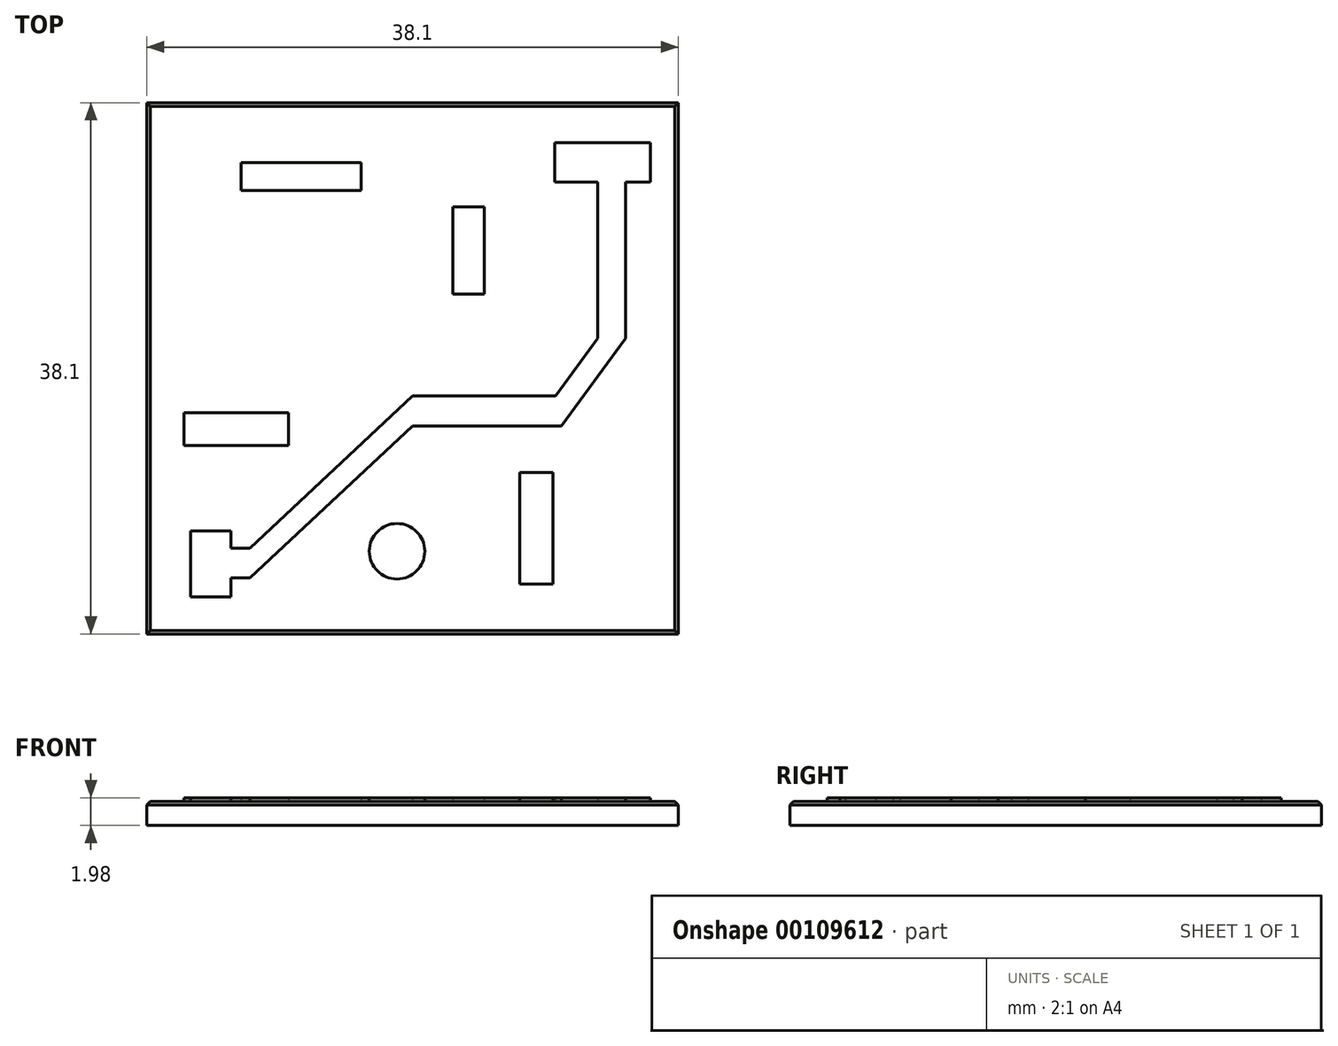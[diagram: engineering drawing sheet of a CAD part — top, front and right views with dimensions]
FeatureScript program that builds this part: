
annotation { "Feature Type Name" : "Feature", "Feature Type Description" : "" }
export const myFeature = defineFeature(function(context is Context, id is Id, definition is map)
    precondition{}
    {
        {
            var Q0;
            Q0=qCreatedBy(makeId("Top.planeOp"),FACE);
            var sketch = newSketch(context, id + "F0", { "sketchPlane" : qUnion([Q0])});
            skLineSegment(sketch, "E0.bottom", {"start": v(19.05, 19.05) * mm, "end": v(-19.05, 19.05) * mm});
            skLineSegment(sketch, "E0.top", {"start": v(19.05, -19.05) * mm, "end": v(-19.05, -19.05) * mm});
            skLineSegment(sketch, "E0.left", {"start": v(19.05, 19.05) * mm, "end": v(19.05, -19.05) * mm});
            skLineSegment(sketch, "E0.right", {"start": v(-19.05, 19.05) * mm, "end": v(-19.05, -19.05) * mm});
            skPoint(sketch, "E0.middle", {"position": v(0, 0) * mm});
            skSolve(sketch);
        }
        {
            var Q0;
            Q0=makeQuery(id+"F0.imprint","IMPRINT",FACE,{"disambiguationData":[TD([[makeQuery(id+"F0.imprint","IMPRINT",EDGE,{"derivedFrom":sQuery(id+"F0.wireOp",EDGE,"E0.bottom")}),1.0]])]});
            extrude(context, id + "F1", {"entities" : qUnion([Q0]), "depth" : 1.73 * mm});
        }
        {
            var Q0;
            Q0=makeQuery(id+"F1.opExtrude","CAP_EDGE",EDGE,{"disambiguationData":[OSD([sQuery(id+"F0.wireOp",EDGE,"E0.top")])],"isStart":false});
            var Q1;
            Q1=makeQuery(id+"F1.opExtrude","CAP_EDGE",EDGE,{"disambiguationData":[OSD([sQuery(id+"F0.wireOp",EDGE,"E0.right")])],"isStart":false});
            var Q2;
            Q2=makeQuery(id+"F1.opExtrude","CAP_EDGE",EDGE,{"disambiguationData":[OSD([sQuery(id+"F0.wireOp",EDGE,"E0.bottom")])],"isStart":false});
            var Q3;
            Q3=makeQuery(id+"F1.opExtrude","CAP_EDGE",EDGE,{"disambiguationData":[OSD([sQuery(id+"F0.wireOp",EDGE,"E0.left")])],"isStart":false});
            chamfer(context, id + "F2", {"entities" : qUnion([Q0, Q1, Q2, Q3]), "width" : 0.25 * mm, "tangentPropagation" : true});
        }
        {
            var Q0;
            Q0=makeQuery(id+"F1.opExtrude","CAP_FACE",FACE,{"disambiguationData":[OSD([sQuery(id+"F0.wireOp",EDGE,"E0.bottom"),sQuery(id+"F0.wireOp",EDGE,"E0.top"),sQuery(id+"F0.wireOp",EDGE,"E0.left"),sQuery(id+"F0.wireOp",EDGE,"E0.right")])],"isStart":false});
            var sketch = newSketch(context, id + "F3", { "sketchPlane" : qUnion([Q0])});
            skLineSegment(sketch, "E1.bottom", {"start": v(-15.9, -11.66) * mm, "end": v(-13, -11.66) * mm});
            skLineSegment(sketch, "E1.top", {"start": v(-15.9, -16.4) * mm, "end": v(-13, -16.4) * mm});
            skLineSegment(sketch, "E1.left", {"start": v(-15.9, -11.66) * mm, "end": v(-15.9, -16.4) * mm});
            skLineSegment(sketch, "E1.right", {"start": v(-13, -11.66) * mm, "end": v(-13, -16.4) * mm});
            skLineSegment(sketch, "E2", {"start": v(-13, -12.89) * mm, "end": v(-11.65, -12.89) * mm});
            skLineSegment(sketch, "E3", {"start": v(-13, -14.03) * mm, "end": v(-11.65, -14.03) * mm});
            skLineSegment(sketch, "E4", {"start": v(-13, -15.04) * mm, "end": v(-11.65, -15.04) * mm});
            skLineSegment(sketch, "E5", {"start": v(-11.65, -12.89) * mm, "end": v(0, -1.98) * mm});
            skLineSegment(sketch, "E6", {"start": v(-11.65, -14.03) * mm, "end": v(0, -3.12) * mm});
            skLineSegment(sketch, "E7", {"start": v(-11.65, -15.04) * mm, "end": v(0, -4.13) * mm});
            skLineSegment(sketch, "E8", {"start": v(0, -1.98) * mm, "end": v(10.25, -1.98) * mm});
            skLineSegment(sketch, "E9", {"start": v(0, -4.13) * mm, "end": v(10.67, -4.13) * mm});
            skLineSegment(sketch, "E10", {"start": v(0, -3.12) * mm, "end": v(10.67, -3.12) * mm});
            skLineSegment(sketch, "E11.bottom", {"start": v(10.19, 16.17) * mm, "end": v(17.05, 16.17) * mm});
            skLineSegment(sketch, "E11.top", {"start": v(10.19, 13.37) * mm, "end": v(17.05, 13.37) * mm});
            skLineSegment(sketch, "E11.left", {"start": v(10.19, 16.17) * mm, "end": v(10.19, 13.37) * mm});
            skLineSegment(sketch, "E11.right", {"start": v(17.05, 16.17) * mm, "end": v(17.05, 13.37) * mm});
            skLineSegment(sketch, "E12", {"start": v(12.03, 13.37) * mm, "end": v(12.03, 11.34) * mm});
            skLineSegment(sketch, "E13", {"start": v(13.28, 13.37) * mm, "end": v(13.28, 11.34) * mm});
            skLineSegment(sketch, "E14", {"start": v(15.27, 13.37) * mm, "end": v(15.27, 11.52) * mm});
            skLineSegment(sketch, "E15", {"start": v(14.54, 13.37) * mm, "end": v(14.54, 11.34) * mm});
            skLineSegment(sketch, "E16", {"start": v(15.27, 11.52) * mm, "end": v(15.27, 2.14) * mm});
            skLineSegment(sketch, "E17", {"start": v(15.27, 2.14) * mm, "end": v(10.67, -4.13) * mm});
            skLineSegment(sketch, "E18", {"start": v(14.54, 11.34) * mm, "end": v(14.54, 2.15) * mm});
            skLineSegment(sketch, "E19", {"start": v(14.54, 2.15) * mm, "end": v(10.67, -3.12) * mm});
            skLineSegment(sketch, "E20", {"start": v(13.28, 11.34) * mm, "end": v(13.28, 2.15) * mm});
            skLineSegment(sketch, "E21", {"start": v(13.28, 2.15) * mm, "end": v(10.25, -1.98) * mm});
            skLineSegment(sketch, "E22", {"start": v(12.03, 11.34) * mm, "end": v(4, 2.25) * mm});
            skLineSegment(sketch, "E23", {"start": v(4, 2.25) * mm, "end": v(-10.6, 2.25) * mm});
            skLineSegment(sketch, "E24", {"start": v(-10.6, 2.25) * mm, "end": v(-15.44, 6.7) * mm});
            skLineSegment(sketch, "E25", {"start": v(-15.44, 6.7) * mm, "end": v(-15.44, 18.8) * mm});
            skPoint(sketch, "E26.oppositeSnap0", {"position": v(-15.44, 12.75) * mm});
            skLineSegment(sketch, "E26.bottom", {"start": v(-12.28, 14.75) * mm, "end": v(-3.67, 14.75) * mm});
            skLineSegment(sketch, "E26.top", {"start": v(-12.28, 12.75) * mm, "end": v(-3.67, 12.75) * mm});
            skLineSegment(sketch, "E26.left", {"start": v(-12.28, 14.75) * mm, "end": v(-12.28, 12.75) * mm});
            skLineSegment(sketch, "E26.right", {"start": v(-3.67, 14.75) * mm, "end": v(-3.67, 12.75) * mm});
            skLineSegment(sketch, "E27.bottom", {"start": v(7.7, -7.49) * mm, "end": v(10.05, -7.49) * mm});
            skLineSegment(sketch, "E27.top", {"start": v(7.7, -15.48) * mm, "end": v(10.05, -15.48) * mm});
            skLineSegment(sketch, "E27.left", {"start": v(7.7, -7.49) * mm, "end": v(7.7, -15.48) * mm});
            skLineSegment(sketch, "E27.right", {"start": v(10.05, -7.49) * mm, "end": v(10.05, -15.48) * mm});
            skLineSegment(sketch, "E28.bottom", {"start": v(-8.9, -3.18) * mm, "end": v(-16.38, -3.18) * mm});
            skLineSegment(sketch, "E28.top", {"start": v(-8.9, -5.54) * mm, "end": v(-16.38, -5.54) * mm});
            skLineSegment(sketch, "E28.left", {"start": v(-8.9, -3.18) * mm, "end": v(-8.9, -5.54) * mm});
            skLineSegment(sketch, "E28.right", {"start": v(-16.38, -3.18) * mm, "end": v(-16.38, -5.54) * mm});
            skLineSegment(sketch, "E29.bottom", {"start": v(2.88, 11.57) * mm, "end": v(5.14, 11.57) * mm});
            skLineSegment(sketch, "E29.top", {"start": v(2.88, 5.32) * mm, "end": v(5.14, 5.32) * mm});
            skLineSegment(sketch, "E29.left", {"start": v(2.88, 11.57) * mm, "end": v(2.88, 5.32) * mm});
            skLineSegment(sketch, "E29.right", {"start": v(5.14, 11.57) * mm, "end": v(5.14, 5.32) * mm});
            skCircle(sketch, "E30", {"center": v(-1.11, -13.12) * mm, "radius": 1.99 * mm});
            skSolve(sketch);
        }
        {
            var Q0;
            Q0 = qSketchRegion(id + "F3", true);
            extrude(context, id + "F4", {"entities" : qUnion([Q0]), "operationType" : NewBodyOperationType.ADD, "depth" : 0.25 * mm});
        }
    });
